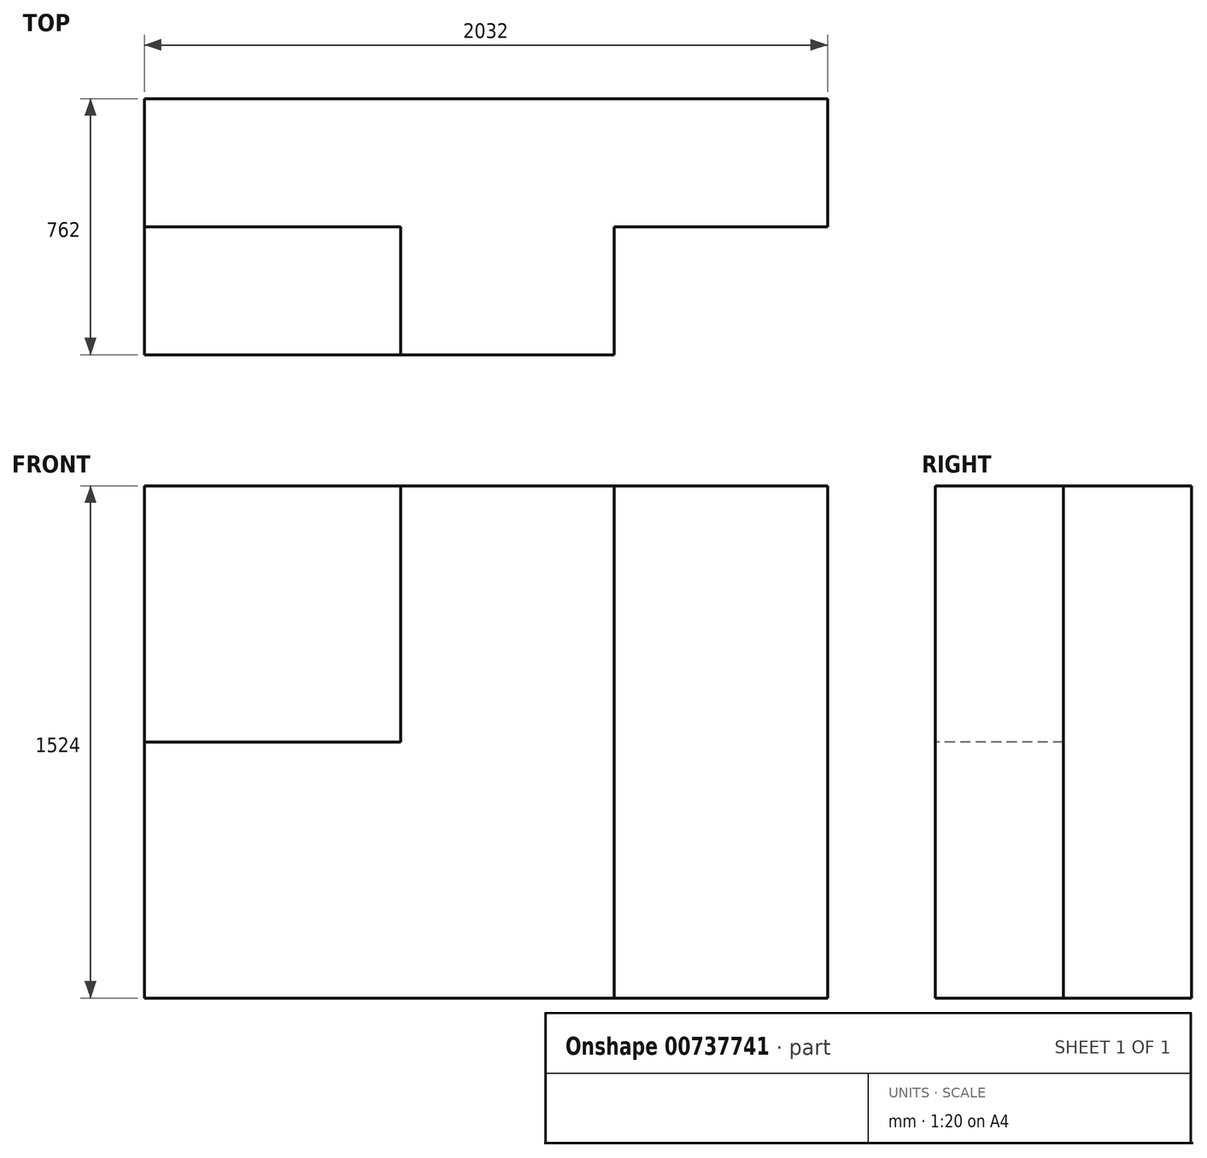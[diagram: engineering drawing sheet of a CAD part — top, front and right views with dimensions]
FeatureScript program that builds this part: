
annotation { "Feature Type Name" : "Feature", "Feature Type Description" : "" }
export const myFeature = defineFeature(function(context is Context, id is Id, definition is map)
    precondition{}
    {
        {
            var Q0;
            Q0=qCreatedBy(makeId("Front.planeOp"),FACE);
            var sketch = newSketch(context, id + "F0", { "sketchPlane" : qUnion([Q0])});
            skLineSegment(sketch, "E0.bottom", {"start": v(-1016, -762) * mm, "end": v(1016, -762) * mm});
            skLineSegment(sketch, "E0.top", {"start": v(-1016, 762) * mm, "end": v(1016, 762) * mm});
            skLineSegment(sketch, "E0.left", {"start": v(-1016, -762) * mm, "end": v(-1016, 762) * mm});
            skLineSegment(sketch, "E0.right", {"start": v(1016, -762) * mm, "end": v(1016, 762) * mm});
            skPoint(sketch, "E0.middle", {"position": v(0, 0) * mm});
            skSolve(sketch);
        }
        {
            var Q0;
            Q0=makeQuery(id+"F0.imprint","IMPRINT",FACE,{"disambiguationData":[TD([[makeQuery(id+"F0.imprint","IMPRINT",EDGE,{"derivedFrom":sQuery(id+"F0.wireOp",EDGE,"E0.bottom")}),1.0]])]});
            extrude(context, id + "F1", {"entities" : qUnion([Q0]), "depth" : 381 * mm, "offsetDistance" : 25.4 * mm});
        }
        {
            var Q0;
            Q0=makeQuery(id+"F1.opExtrude","CAP_FACE",FACE,{"disambiguationData":[OSD([sQuery(id+"F0.wireOp",EDGE,"E0.bottom"),sQuery(id+"F0.wireOp",EDGE,"E0.top"),sQuery(id+"F0.wireOp",EDGE,"E0.left"),sQuery(id+"F0.wireOp",EDGE,"E0.right")])],"isStart":false});
            var sketch = newSketch(context, id + "F2", { "sketchPlane" : qUnion([Q0])});
            skLineSegment(sketch, "E1.bottom", {"start": v(-1016, 762) * mm, "end": v(381, 762) * mm});
            skLineSegment(sketch, "E1.top", {"start": v(-1016, -762) * mm, "end": v(381, -762) * mm});
            skLineSegment(sketch, "E1.left", {"start": v(-1016, 762) * mm, "end": v(-1016, -762) * mm});
            skLineSegment(sketch, "E1.right", {"start": v(381, 762) * mm, "end": v(381, -762) * mm});
            skSolve(sketch);
        }
        {
            var Q0;
            Q0=makeQuery(id+"F2.imprint","IMPRINT",FACE,{"disambiguationData":[TD([[makeQuery(id+"F2.imprint","IMPRINT",EDGE,{"derivedFrom":sQuery(id+"F2.wireOp",EDGE,"E1.bottom")}),-1.0]])]});
            extrude(context, id + "F3", {"entities" : qUnion([Q0]), "operationType" : NewBodyOperationType.ADD, "depth" : 381 * mm, "offsetDistance" : 25.4 * mm});
        }
        {
            var Q0;
            Q0=makeQuery(id+"F3.opExtrude","CAP_FACE",FACE,{"disambiguationData":[OSD([sQuery(id+"F2.wireOp",EDGE,"E1.bottom"),sQuery(id+"F2.wireOp",EDGE,"E1.top"),sQuery(id+"F2.wireOp",EDGE,"E1.left"),sQuery(id+"F2.wireOp",EDGE,"E1.right")])],"isStart":false});
            var sketch = newSketch(context, id + "F4", { "sketchPlane" : qUnion([Q0])});
            skLineSegment(sketch, "E2.bottom", {"start": v(-1016, 762) * mm, "end": v(-254, 762) * mm});
            skLineSegment(sketch, "E2.top", {"start": v(-1016, 0) * mm, "end": v(-254, 0) * mm});
            skLineSegment(sketch, "E2.left", {"start": v(-1016, 762) * mm, "end": v(-1016, 0) * mm});
            skLineSegment(sketch, "E2.right", {"start": v(-254, 762) * mm, "end": v(-254, 0) * mm});
            skSolve(sketch);
        }
        {
            var Q0;
            Q0=makeQuery(id+"F4.imprint","IMPRINT",FACE,{"disambiguationData":[TD([[makeQuery(id+"F4.imprint","IMPRINT",EDGE,{"derivedFrom":sQuery(id+"F4.wireOp",EDGE,"E2.bottom")}),-1.0]])]});
            extrude(context, id + "F5", {"entities" : qUnion([Q0]), "operationType" : NewBodyOperationType.ADD, "depth" : 127 * mm, "offsetDistance" : 25.4 * mm});
        }
        {
            var Q0;
            Q0=makeQuery(id+"F5.opExtrude","CAP_FACE",FACE,{"disambiguationData":[OSD([sQuery(id+"F4.wireOp",EDGE,"E2.bottom"),sQuery(id+"F4.wireOp",EDGE,"E2.top"),sQuery(id+"F4.wireOp",EDGE,"E2.left"),sQuery(id+"F4.wireOp",EDGE,"E2.right")])],"isStart":false});
            var Q1;
            Q1=makeQuery(id+"F1.opExtrude","CAP_FACE",FACE,{"disambiguationData":[OSD([sQuery(id+"F0.wireOp",EDGE,"E0.bottom"),sQuery(id+"F0.wireOp",EDGE,"E0.top"),sQuery(id+"F0.wireOp",EDGE,"E0.left"),sQuery(id+"F0.wireOp",EDGE,"E0.right")])],"isStart":false});
            extrude(context, id + "F6", {"entities" : qUnion([Q0]), "operationType" : NewBodyOperationType.REMOVE, "endBound" : BoundingType.UP_TO_SURFACE, "oppositeDirection" : true, "depth" : 381 * mm, "endBoundEntityFace" : qUnion([Q1]), "offsetDistance" : 25.4 * mm});
        }
    });
